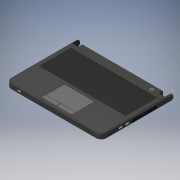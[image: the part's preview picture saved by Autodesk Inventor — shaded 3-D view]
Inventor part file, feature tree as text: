
AUTODESK INVENTOR PART (.ipt)
format: ipt  version: 2025 (Build 290162000, 162)  size: 428,032 bytes
history: native  units: in
note: dims shown in document units (in); Inventor stores cm internally (conversion verified against a paired STEP export)
features: sketch x24, extrude x21, chamfer x3, hole x2, other x1, pattern_linear x1
ambient origin geometry x8: Origin, YZ Plane, XZ Plane, XY Plane, X Axis, Y Axis, Z Axis, Center Point
bodies: Solid1 (feature_tree)
feature tree (52):
  other  "BOARD"
  chamfer  "HINGE CHAMFER"  Distance=0.7874in
  extrude  "TOUCH PAD"  Depth=4.1339in
  extrude  "LEFT BUTTON"  Depth=0.1969in
  extrude  "RIGHT BUTTON"  Depth=2.0472in
  extrude  "KEYBOARD BASE"  Depth=0.1969in
  chamfer  "KEYBOARD CHAMFER"  Distance=0.0236in
  extrude  "CUT"  Depth=11.811in
  extrude  "ROUND BASE"  Depth=0.0118in TaperAngle=0.0deg
  extrude  "ROUND BASE 1"  Depth=12.9921in TaperAngle=0.0deg
  chamfer  "BOARD BASE"  Distance=0.1772in
  extrude  "POWER BUTTON"  Depth=0.0984in TaperAngle=45.0deg
  hole  "POWER BUTTON 1"  [1 undecoded]
  hole  "CHARGING PORT"  [1 undecoded]
  extrude  "HEAT SINK"  Depth=0.1969in TaperAngle=0.0deg
  pattern_linear  "HEAT SINK PATTERN"  Count1=4  [1 undecoded]
  extrude  "HDMI PORT"  Depth=0.0984in
  extrude  "HDMI SLOT"  Depth=0.1969in
  extrude  "USB PORT"  Depth=3.5433in
  extrude  "USB SLOT"  Depth=0.0079in TaperAngle=0.0deg
  extrude  "MEMORY SLOT"  Depth=0.1969in
  extrude  "DISK HOLDER"  Depth=0.0591in
  extrude  "DISK HOLDER BUTTON"  Depth=0.0197in
  extrude  "BATTERY INDICATOR"  Depth=0.002in TaperAngle=0.0deg
  sketch  "Sketch1"  dims[d19=10.9843in]
  sketch  "Sketch2"  dims[d20=0.4331in]
  sketch  "Sketch3"  dims[d21=0.8268in]
  sketch  "Sketch4"  dims[d22=0.8661in d23=0.7874in d24=0.0in]
  sketch  "Sketch5"  dims[d25=0.0984in d26=0.0492in d27=45.0deg d32=4.1339in]
  sketch  "Sketch6"  dims[d33=3.1496in d34=0.1969in]
  sketch  "Sketch7"  dims[d35=0.0197in d36=0.0in d39=2.0472in]
  sketch  "Sketch8"  dims[d40=0.5906in d41=0.1969in d42=0.0236in d43=0.0in]
  sketch  "Sketch9"  dims[d48=0.0236in d49=0.0in d57=11.811in]
  sketch  "Sketch10"  dims[d58=4.3307in d59=0.0118in d60=0.0in]
  sketch  "Sketch11"  dims[d61=0.0118in d62=0.0492in d63=45.0deg d64=12.9921in d65=0.0in d66=0.1772in d67=0.0in]
  sketch  "Sketch12"  dims[d68=0.1772in d69=0.0in d70=0.0984in d71=0.0492in d72=45.0deg]
  sketch  "Sketch13"  dims[d73=0.5906in d74=0.002in d75=0.0in]
  sketch  "Sketch14"  dims[d76=0.0787in d77=0.2953in d78=0.1476in d79=0.0984in d80=90.0deg d81=0.002in d82=0.8108in]
  sketch  "Sketch15"  dims[d85=0.2559in d86=0.2953in d87=0.3346in d88=0.0039in d89=90.0deg d90=0.1969in d91=0.0in d97=0.0787in d98=0.0in]
  sketch  "Sketch16"  dims[d99=5.9055in d101=0.1575in d111=0.1969in d112=0.0in]
  sketch  "Sketch17"  dims[d115=0.1969in d116=0.0in]
  sketch  "Sketch18"  dims[d121=0.1969in d122=0.0in]
  sketch  "Sketch19"  dims[d126=0.4882in]
  sketch  "Sketch26"  dims[d148=0.4921in d150=3.5433in d151=0.0079in d152=0.0in d158=0.1969in d159=0.0591in d160=0.0197in d161=0.002in d162=0.0in d172=0.0in d173=0.1969in d174=0.4882in d175=0.0197in d177=0.0in d178=0.1969in d180=0.0in d181=0.1969in d182=0.4882in d183=0.0197in d185=0.0in d186=0.1969in d190=0.4724in d191=0.1575in d192=0.0787in d193=0.002in d194=0.0in]
  sketch  "Sketch22"  dims[d127=0.0197in]
  sketch  "Sketch23"  dims[d128=0.1969in d129=0.0in d134=1.5748in]
  sketch  "Sketch24"  dims[d136=0.1969in d137=0.0984in]
  sketch  "Sketch25"  dims[d138=0.1969in d139=0.0in d147=0.1969in]
  extrude  "USB PORT 1"  Depth=0.1969in TaperAngle=0.0deg
  extrude  "USB SLOT 1"  Depth=0.4882in TaperAngle=0.0deg
  extrude  "USB PORT 2"  Depth=0.1969in TaperAngle=0.0deg
  extrude  "USB SLOT 2"  Depth=0.4882in TaperAngle=0.0deg
note: 3 required parameter values undecoded (feature->parameter linkage not recoverable at this tier; creation-order binding heuristic only, values carry confidence <= 0.55)
